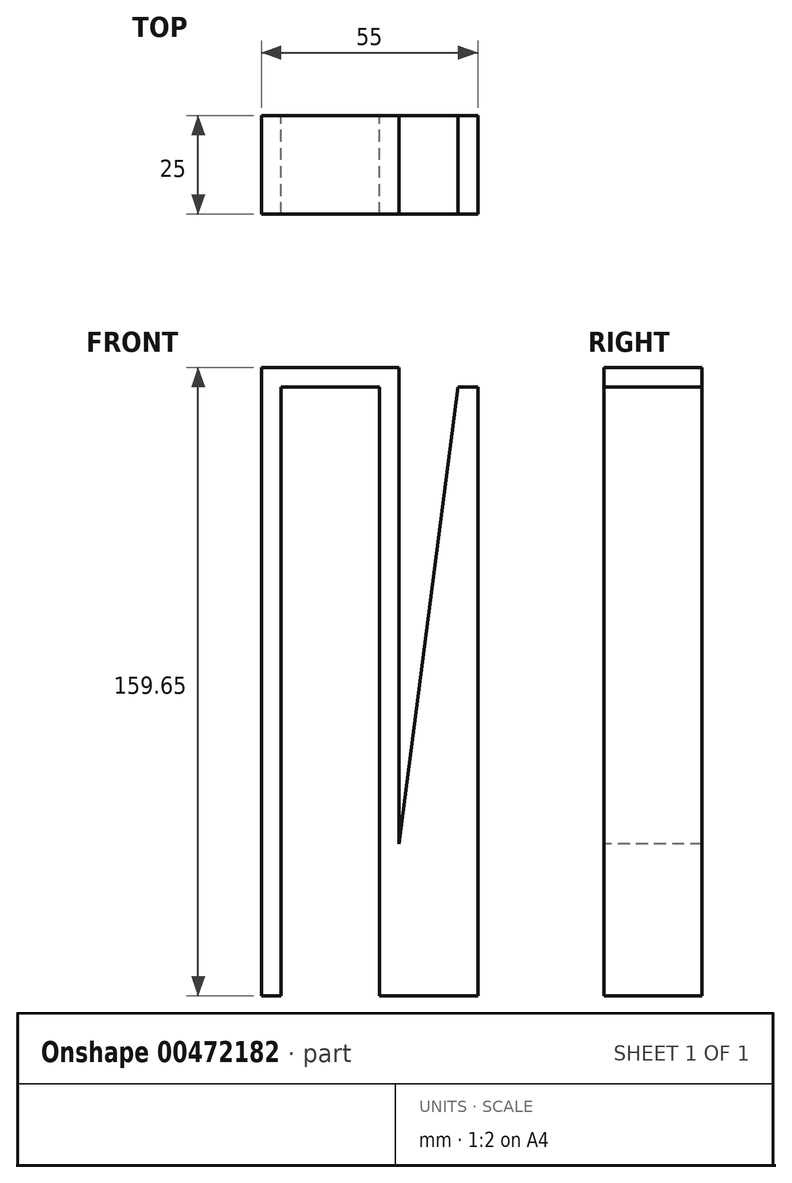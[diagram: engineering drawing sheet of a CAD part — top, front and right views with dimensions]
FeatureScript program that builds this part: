
annotation { "Feature Type Name" : "Feature", "Feature Type Description" : "" }
export const myFeature = defineFeature(function(context is Context, id is Id, definition is map)
    precondition{}
    {
        {
            var Q0;
            Q0=qCreatedBy(makeId("Front.planeOp"),FACE);
            var sketch = newSketch(context, id + "F0", { "sketchPlane" : qUnion([Q0])});
            skLineSegment(sketch, "E0", {"start": v(0, 61.63) * mm, "end": v(0, -93.02) * mm});
            skLineSegment(sketch, "E1.1.0.0", {"start": v(25, 61.63) * mm, "end": v(25, -93.02) * mm});
            skLineSegment(sketch, "E1.2.0.0", {"start": v(50, 61.63) * mm, "end": v(50, -93.02) * mm});
            skLineSegment(sketch, "E1.direction1", {"start": v(0, -93.02) * mm, "end": v(25, -93.02) * mm, "construction": true});
            skLineSegment(sketch, "E2", {"start": v(0, 61.63) * mm, "end": v(25, 61.63) * mm});
            skLineSegment(sketch, "E3", {"start": v(25, -93.02) * mm, "end": v(50, -93.02) * mm});
            skLineSegment(sketch, "E4.0", {"start": v(-5, 66.63) * mm, "end": v(-5, -93.02) * mm});
            skLineSegment(sketch, "E4.1", {"start": v(45, 61.63) * mm, "end": v(45, -88.02) * mm});
            skLineSegment(sketch, "E4.2", {"start": v(30, -88.02) * mm, "end": v(45, -88.02) * mm});
            skLineSegment(sketch, "E4.3", {"start": v(30, 66.63) * mm, "end": v(30, -88.02) * mm});
            skLineSegment(sketch, "E4.4", {"start": v(-5, 66.63) * mm, "end": v(30, 66.63) * mm});
            skLineSegment(sketch, "E5", {"start": v(-5, -93.02) * mm, "end": v(0, -93.02) * mm});
            skLineSegment(sketch, "E6", {"start": v(50, 61.63) * mm, "end": v(45, 61.63) * mm});
            skSolve(sketch);
        }
        {
            var Q0;
            Q0 = qSketchRegion(id + "F0", true);
            extrude(context, id + "F1", {"entities" : qUnion([Q0]), "depth" : 25 * mm});
        }
        {
            var Q1;
            Q1=makeQuery(id+"F1.opExtrude","SWEPT_FACE",FACE,{"disambiguationData":[OSD([sQuery(id+"F0.wireOp",EDGE,"E6")])]});
            var Q2;
            Q2=makeQuery(id+"F1.opExtrude","SWEPT_FACE",FACE,{"disambiguationData":[OSD([sQuery(id+"F0.wireOp",EDGE,"E3")])]});
            var Q3;
            Q3=makeQuery(id+"F1.opExtrude","CAP_EDGE",EDGE,{"disambiguationData":[OSD([sQuery(id+"F0.wireOp",EDGE,"E1.2.0.0")])],"isStart":false});
            var Q4;
            Q4=makeQuery(id+"F1.opExtrude","CAP_EDGE",EDGE,{"disambiguationData":[OSD([sQuery(id+"F0.wireOp",EDGE,"E1.2.0.0")])],"isStart":true});
            loft(context, id + "F2", {"operationType" : NewBodyOperationType.ADD, "addGuides" : true, "sheetProfilesArray" : [{ "sheetProfileEntities" : qUnion([Q1]) }, { "sheetProfileEntities" : qUnion([Q2]) }], "guidesArray" : [{ "guideEntities" : qUnion([Q3]), "guideDerivativeType" : LoftGuideDerivativeType.DEFAULT, "guideDerivativeMagnitude" : 1 }, { "guideEntities" : qUnion([Q4]), "guideDerivativeType" : LoftGuideDerivativeType.DEFAULT, "guideDerivativeMagnitude" : 1 }]});
        }
    });
